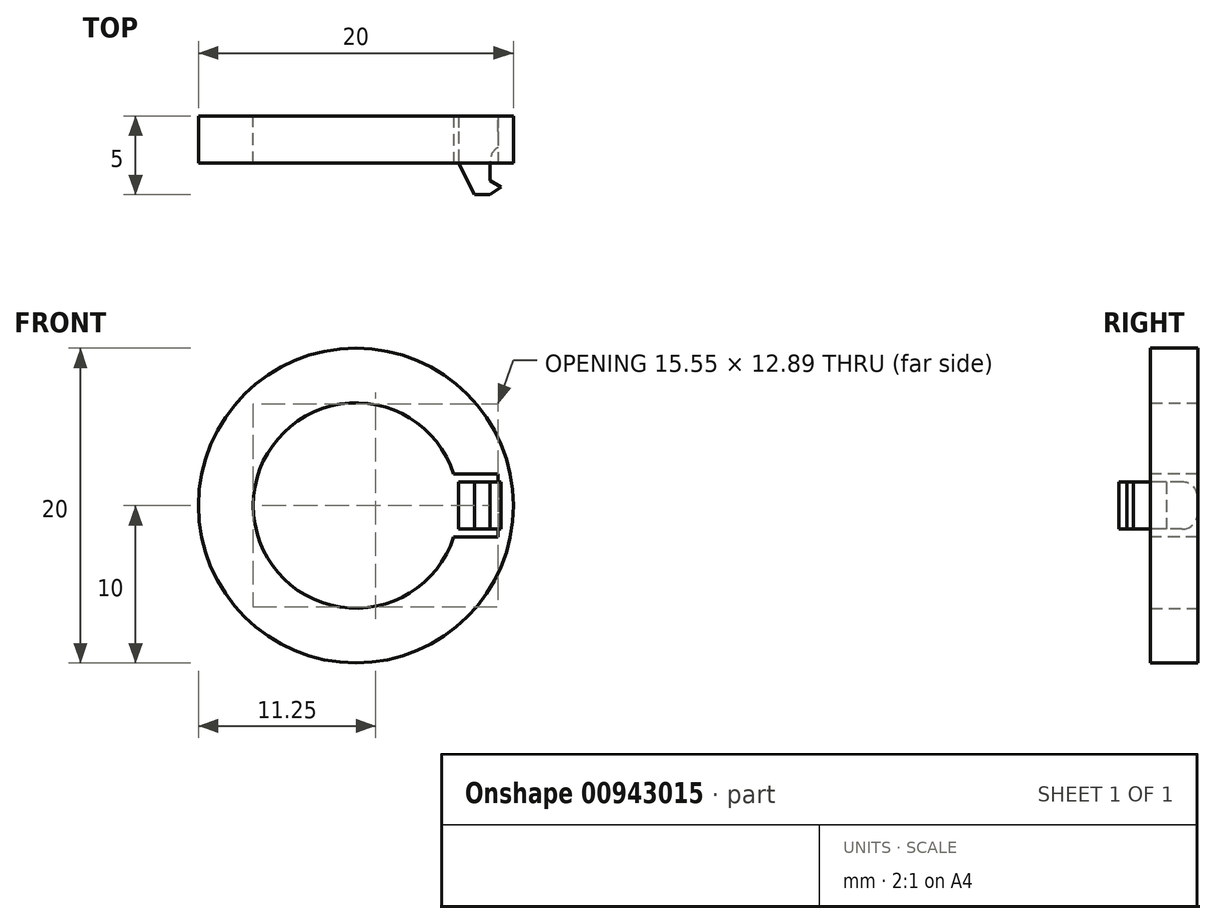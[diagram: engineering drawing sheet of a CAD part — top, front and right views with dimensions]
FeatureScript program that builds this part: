
annotation { "Feature Type Name" : "Feature", "Feature Type Description" : "" }
export const myFeature = defineFeature(function(context is Context, id is Id, definition is map)
    precondition{}
    {
        {
            var Q0;
            Q0=qCreatedBy(makeId("Front.planeOp"),FACE);
            var sketch = newSketch(context, id + "F0", { "sketchPlane" : qUnion([Q0])});
            skCircle(sketch, "E0", {"center": v(0, 0) * mm, "radius": 6.53 * mm});
            skCircle(sketch, "E1", {"center": v(0, 0) * mm, "radius": 10 * mm});
            skPoint(sketch, "E2", {"position": v(6.53, 0) * mm});
            skSolve(sketch);
        }
        {
            var Q0;
            Q0 = qSketchRegion(id + "F0", true);
            extrude(context, id + "F1", {"entities" : qUnion([Q0]), "depth" : 3 * mm, "offsetDistance" : 25 * mm});
        }
        {
            var Q0;
            Q0=qCreatedBy(makeId("Top.planeOp"),FACE);
            var sketch = newSketch(context, id + "F2", { "sketchPlane" : qUnion([Q0])});
            skLineSegment(sketch, "E3.bottom", {"start": v(6.53, -3) * mm, "end": v(8.53, -3) * mm});
            skLineSegment(sketch, "E3.top", {"start": v(7.53, -5) * mm, "end": v(8.53, -5) * mm});
            skLineSegment(sketch, "E3.left", {"start": v(6.53, -3) * mm, "end": v(7.53, -5) * mm});
            skLineSegment(sketch, "E3.right", {"start": v(8.53, -3) * mm, "end": v(8.53, -4.1) * mm});
            skLineSegment(sketch, "E4", {"start": v(8.53, -4.1) * mm, "end": v(9.23, -4.5) * mm});
            skLineSegment(sketch, "E5", {"start": v(9.23, -4.5) * mm, "end": v(8.53, -5) * mm});
            skLineSegment(sketch, "E6", {"start": v(0, 6.77) * mm, "end": v(0, -9.64) * mm, "construction": true});
            skSolve(sketch);
        }
        {
            var Q0;
            Q0=makeQuery(id+"F2.imprint","IMPRINT",FACE,{"disambiguationData":[TD([[makeQuery(id+"F2.imprint","IMPRINT",EDGE,{"derivedFrom":sQuery(id+"F2.wireOp",EDGE,"E3.bottom")}),-1.0]])]});
            extrude(context, id + "F3", {"entities" : qUnion([Q0]), "operationType" : NewBodyOperationType.ADD, "endBound" : BoundingType.SYMMETRIC, "depth" : 3 * mm, "offsetDistance" : 25 * mm});
        }
        {
            var Q0;
            Q0=makeQuery(id+"F1.opExtrude","CAP_FACE",FACE,{"disambiguationData":[OSD([sQuery(id+"F0.wireOp",EDGE,"E0"),sQuery(id+"F0.wireOp",EDGE,"E1")])],"isStart":false});
            var sketch = newSketch(context, id + "F4", { "sketchPlane" : qUnion([Q0])});
            skLineSegment(sketch, "E7", {"start": v(6.21, 2) * mm, "end": v(8.53, 2) * mm});
            skLineSegment(sketch, "E8", {"start": v(8.53, 2) * mm, "end": v(8.53, 1.5) * mm});
            skLineSegment(sketch, "E9.MirrorCS", {"start": v(6.21, -2) * mm, "end": v(8.53, -2) * mm});
            skLineSegment(sketch, "E10.MirrorCS", {"start": v(8.53, -2) * mm, "end": v(8.53, -1.5) * mm});
            skLineSegment(sketch, "E11", {"start": v(8.53, 2) * mm, "end": v(9.03, 2) * mm});
            skLineSegment(sketch, "E12", {"start": v(9.03, 2) * mm, "end": v(9.03, -2) * mm});
            skLineSegment(sketch, "E13", {"start": v(9.03, -2) * mm, "end": v(8.53, -2) * mm});
            skLineSegment(sketch, "E14", {"start": v(8.53, 1.5) * mm, "end": v(9.03, 1.5) * mm});
            skLineSegment(sketch, "E15", {"start": v(8.53, -1.5) * mm, "end": v(9.03, -1.5) * mm});
            skSolve(sketch);
        }
        {
            var Q0;
            {var subQ12=sQuery(id+"F4.wireOp",EDGE,"E7");Q0=makeQuery(id+"F4.imprint","IMPRINT",FACE,{"disambiguationData":[TD([[makeQuery(id+"F4.imprint","IMPRINT",EDGE,{"derivedFrom":subQ12}),-1.0]])]});}
            var Q1;
            {var subQ12=sQuery(id+"F4.wireOp",EDGE,"E9.MirrorCS");Q1=makeQuery(id+"F4.imprint","IMPRINT",FACE,{"disambiguationData":[TD([[makeQuery(id+"F4.imprint","IMPRINT",EDGE,{"derivedFrom":subQ12}),1.0]])]});}
            var Q2;
            Q2=makeQuery(id+"F4.imprint","IMPRINT",FACE,{"disambiguationData":[TD([[makeQuery(id+"F4.imprint","IMPRINT",EDGE,{"derivedFrom":sQuery(id+"F4.wireOp",EDGE,"E8")}),1.0]])]});
            var Q3;
            Q3=makeQuery(id+"F4.imprint","IMPRINT",FACE,{"disambiguationData":[TD([[makeQuery(id+"F4.imprint","IMPRINT",EDGE,{"derivedFrom":sQuery(id+"F4.wireOp",EDGE,"E10.MirrorCS")}),-1.0]])]});
            extrude(context, id + "F5", {"entities" : qUnion([Q0, Q1, Q2, Q3]), "operationType" : NewBodyOperationType.REMOVE, "oppositeDirection" : true, "depth" : 25 * mm, "offsetDistance" : 25 * mm});
        }
        {
            var Q0;
            {var subQ0=sQuery(id+"F4.wireOp",EDGE,"E14");Q0=makeQuery(id+"F4.imprint","IMPRINT",FACE,{"disambiguationData":[TD([[makeQuery(id+"F4.imprint","IMPRINT",EDGE,{"derivedFrom":subQ0}),-1.0]])]});}
            extrude(context, id + "F6", {"entities" : qUnion([Q0]), "operationType" : NewBodyOperationType.REMOVE, "oppositeDirection" : true, "depth" : 1 * mm, "offsetDistance" : 25 * mm});
        }
        {
            var Q0;
            {var subQ0=sQuery(id+"F0.wireOp",EDGE,"E0");var subQ2=sQuery(id+"F2.wireOp",EDGE,"E5");var subQ3=sQuery(id+"F2.wireOp",EDGE,"E4");var subQ4=sQuery(id+"F2.wireOp",EDGE,"E3.right");var subQ5=sQuery(id+"F2.wireOp",EDGE,"E3.left");var subQ6=sQuery(id+"F2.wireOp",EDGE,"E3.top");var subQ7=sQuery(id+"F2.wireOp",EDGE,"E3.bottom");var subQ8=sQuery(id+"F0.wireOp",EDGE,"E1");var subQ11=makeQuery(id+"F3.opExtrude","SWEPT_EDGE",EDGE,{"disambiguationData":[OSD([subQ7,subQ5])]});Q0=makeQuery(id+"F5.boolean.opBoolean","INTERSECT",EDGE,{"derivedFrom":[makeQuery(id+"F1.opExtrude","CAP_FACE",FACE,{"disambiguationData":[OSD([subQ0,subQ8])],"isStart":true}),makeQuery(id+"F5.opExtrude","SWEPT_FACE",FACE,{"disambiguationData":[OSD([subQ7,subQ5]),TDD([makeQuery(id+"F4.imprint","IMPRINT",EDGE,{"derivedFrom":makeQuery(id+"F3.boolean.opBoolean","SPLIT",EDGE,{"disambiguationData":[TD([makeQuery(id+"F3.opExtrude","CAP_FACE",FACE,{"disambiguationData":[OSD([subQ7,subQ6,subQ5,subQ4,subQ3,subQ2])],"isStart":true})])],"derivedFrom":subQ11})})])]}),makeQuery(id+"F5.opExtrude","SWEPT_FACE",FACE,{"disambiguationData":[OSD([subQ7,subQ5]),TDD([makeQuery(id+"F4.imprint","IMPRINT",EDGE,{"derivedFrom":makeQuery(id+"F3.boolean.opBoolean","SPLIT",EDGE,{"disambiguationData":[TD([makeQuery(id+"F3.opExtrude","CAP_FACE",FACE,{"disambiguationData":[OSD([subQ7,subQ6,subQ5,subQ4,subQ3,subQ2])],"isStart":false})])],"derivedFrom":subQ11})})])]})]});}
            fillet(context, id + "F7", {"entities" : qUnion([Q0]), "radius" : 1 * mm, "tangentPropagation" : true, "allowEdgeOverflow" : false});
        }
        {
            var Q0;
            Q0=makeQuery(id+"F6.boolean.opBoolean","COPY",EDGE,{"derivedFrom":makeQuery(id+"F6.opExtrude","CAP_EDGE",EDGE,{"disambiguationData":[OSD([sQuery(id+"F2.wireOp",EDGE,"E3.bottom"),sQuery(id+"F2.wireOp",EDGE,"E3.right")])],"isStart":false})});
            fillet(context, id + "F8", {"entities" : qUnion([Q0]), "radius" : 1 * mm, "tangentPropagation" : true, "allowEdgeOverflow" : false});
        }
        {
            var Q0;
            Q0=qCreatedBy(makeId("Front.planeOp"),FACE);
            cPlane(context, id + "F9", {"entities" : qUnion([Q0]), "cplaneType" : CPlaneType.OFFSET, "offset" : 25 * mm, "width" : 150 * mm, "height" : 150 * mm});
        }
        {
            var Q0;
            Q0=qCreatedBy(id+"F9.planeOp",FACE);
            var sketch = newSketch(context, id + "F10", { "sketchPlane" : qUnion([Q0])});
            skCircle(sketch, "E16", {"center": v(0, 0) * mm, "radius": 10 * mm});
            skCircle(sketch, "E17", {"center": v(0, 0) * mm, "radius": 6.55 * mm});
            skLineSegment(sketch, "E18", {"start": v(-1.75, 6.31) * mm, "end": v(-1.75, 8.61) * mm});
            skLineSegment(sketch, "E19", {"start": v(-1.75, 8.61) * mm, "end": v(1.75, 8.61) * mm});
            skLineSegment(sketch, "E20", {"start": v(1.75, 8.61) * mm, "end": v(1.75, 6.31) * mm});
            skLineSegment(sketch, "E21.1.0", {"start": v(-6.31, -1.75) * mm, "end": v(-8.61, -1.75) * mm});
            skLineSegment(sketch, "E21.1.1", {"start": v(-8.61, -1.75) * mm, "end": v(-8.61, 1.75) * mm});
            skLineSegment(sketch, "E21.1.2", {"start": v(-8.61, 1.75) * mm, "end": v(-6.31, 1.75) * mm});
            skLineSegment(sketch, "E21.2.0", {"start": v(1.75, -6.31) * mm, "end": v(1.75, -8.61) * mm});
            skLineSegment(sketch, "E21.2.1", {"start": v(1.75, -8.61) * mm, "end": v(-1.75, -8.61) * mm});
            skLineSegment(sketch, "E21.2.2", {"start": v(-1.75, -8.61) * mm, "end": v(-1.75, -6.31) * mm});
            skLineSegment(sketch, "E21.3.0", {"start": v(6.31, 1.75) * mm, "end": v(8.61, 1.75) * mm});
            skLineSegment(sketch, "E21.3.1", {"start": v(8.61, 1.75) * mm, "end": v(8.61, -1.75) * mm});
            skLineSegment(sketch, "E21.3.2", {"start": v(8.61, -1.75) * mm, "end": v(6.31, -1.75) * mm});
            skSolve(sketch);
        }
        {
            var Q0;
            Q0 = qSketchRegion(id + "F10", true);
            extrude(context, id + "F11", {"entities" : qUnion([Q0]), "depth" : 2 * mm, "offsetDistance" : 25 * mm});
        }
        {
            var Q0;
            Q0=makeQuery(id+"F11.opExtrude","CAP_FACE",FACE,{"disambiguationData":[OSD([sQuery(id+"F10.wireOp",EDGE,"E16"),sQuery(id+"F10.wireOp",EDGE,"E17"),sQuery(id+"F10.wireOp",EDGE,"E18"),sQuery(id+"F10.wireOp",EDGE,"E19"),sQuery(id+"F10.wireOp",EDGE,"E20"),sQuery(id+"F10.wireOp",EDGE,"E21.1.0"),sQuery(id+"F10.wireOp",EDGE,"E21.1.1"),sQuery(id+"F10.wireOp",EDGE,"E21.1.2"),sQuery(id+"F10.wireOp",EDGE,"E21.2.0"),sQuery(id+"F10.wireOp",EDGE,"E21.2.1"),sQuery(id+"F10.wireOp",EDGE,"E21.2.2"),sQuery(id+"F10.wireOp",EDGE,"E21.3.0"),sQuery(id+"F10.wireOp",EDGE,"E21.3.1"),sQuery(id+"F10.wireOp",EDGE,"E21.3.2")])],"isStart":false});
            var sketch = newSketch(context, id + "F12", { "sketchPlane" : qUnion([Q0])});
            skLineSegment(sketch, "E22", {"start": v(-1.75, 8.61) * mm, "end": v(-1.75, 9.61) * mm});
            skLineSegment(sketch, "E23", {"start": v(-1.75, 9.61) * mm, "end": v(1.75, 9.61) * mm});
            skLineSegment(sketch, "E24", {"start": v(1.75, 9.61) * mm, "end": v(1.75, 8.61) * mm});
            skLineSegment(sketch, "E25.1.0", {"start": v(-8.61, -1.75) * mm, "end": v(-9.61, -1.75) * mm});
            skLineSegment(sketch, "E25.1.1", {"start": v(-9.61, -1.75) * mm, "end": v(-9.61, 1.75) * mm});
            skLineSegment(sketch, "E25.1.2", {"start": v(-9.61, 1.75) * mm, "end": v(-8.61, 1.75) * mm});
            skLineSegment(sketch, "E25.2.0", {"start": v(1.75, -8.61) * mm, "end": v(1.75, -9.61) * mm});
            skLineSegment(sketch, "E25.2.1", {"start": v(1.75, -9.61) * mm, "end": v(-1.75, -9.61) * mm});
            skLineSegment(sketch, "E25.2.2", {"start": v(-1.75, -9.61) * mm, "end": v(-1.75, -8.61) * mm});
            skLineSegment(sketch, "E25.3.0", {"start": v(8.61, 1.75) * mm, "end": v(9.61, 1.75) * mm});
            skLineSegment(sketch, "E25.3.1", {"start": v(9.61, 1.75) * mm, "end": v(9.61, -1.75) * mm});
            skLineSegment(sketch, "E25.3.2", {"start": v(9.61, -1.75) * mm, "end": v(8.61, -1.75) * mm});
            skPoint(sketch, "E25.center", {"position": v(0, 0) * mm});
            skSolve(sketch);
        }
        {
            var Q0;
            Q0=makeQuery(id+"F12.imprint","IMPRINT",FACE,{"disambiguationData":[TD([[makeQuery(id+"F12.imprint","IMPRINT",EDGE,{"derivedFrom":sQuery(id+"F12.wireOp",EDGE,"E22")}),-1.0]])]});
            var Q1;
            Q1=makeQuery(id+"F12.imprint","IMPRINT",FACE,{"disambiguationData":[TD([[makeQuery(id+"F12.imprint","IMPRINT",EDGE,{"derivedFrom":sQuery(id+"F12.wireOp",EDGE,"E25.1.0")}),-1.0]])]});
            var Q2;
            Q2=makeQuery(id+"F12.imprint","IMPRINT",FACE,{"disambiguationData":[TD([[makeQuery(id+"F12.imprint","IMPRINT",EDGE,{"derivedFrom":sQuery(id+"F12.wireOp",EDGE,"E25.3.0")}),-1.0]])]});
            var Q3;
            Q3=makeQuery(id+"F12.imprint","IMPRINT",FACE,{"disambiguationData":[TD([[makeQuery(id+"F12.imprint","IMPRINT",EDGE,{"derivedFrom":sQuery(id+"F12.wireOp",EDGE,"E25.2.0")}),-1.0]])]});
            extrude(context, id + "F13", {"entities" : qUnion([Q0, Q1, Q2, Q3]), "operationType" : NewBodyOperationType.REMOVE, "oppositeDirection" : true, "depth" : 1 * mm, "offsetDistance" : 25 * mm});
        }
        {
            var Q0;
            Q0=qCreatedBy(id+"F9.planeOp",FACE);
            var sketch = newSketch(context, id + "F14", { "sketchPlane" : qUnion([Q0])});
            skCircle(sketch, "E26", {"center": v(0, 0) * mm, "radius": 10.98 * mm});
            skSolve(sketch);
        }
        {
            var Q0;
            Q0 = qSketchRegion(id + "F14", true);
            extrude(context, id + "F15", {"entities" : qUnion([Q0]), "depth" : 2 * mm, "offsetDistance" : 25 * mm});
        }
        {
            var Q0;
            Q0=makeQuery(id+"F11.opExtrude","SWEPT_BODY",BODY,{"disambiguationData":[OSD([sQuery(id+"F10.wireOp",EDGE,"E16"),sQuery(id+"F10.wireOp",EDGE,"E17"),sQuery(id+"F10.wireOp",EDGE,"E18"),sQuery(id+"F10.wireOp",EDGE,"E19"),sQuery(id+"F10.wireOp",EDGE,"E20"),sQuery(id+"F10.wireOp",EDGE,"E21.1.0"),sQuery(id+"F10.wireOp",EDGE,"E21.1.1"),sQuery(id+"F10.wireOp",EDGE,"E21.1.2"),sQuery(id+"F10.wireOp",EDGE,"E21.2.0"),sQuery(id+"F10.wireOp",EDGE,"E21.2.1"),sQuery(id+"F10.wireOp",EDGE,"E21.2.2"),sQuery(id+"F10.wireOp",EDGE,"E21.3.0"),sQuery(id+"F10.wireOp",EDGE,"E21.3.1"),sQuery(id+"F10.wireOp",EDGE,"E21.3.2")])]});
            var Q1;
            Q1=makeQuery(id+"F15.opExtrude","SWEPT_BODY",BODY,{"disambiguationData":[OSD([sQuery(id+"F14.wireOp",EDGE,"E26")])]});
            booleanBodies(context, id + "F16", {"operationType" : BooleanOperationType.SUBTRACTION, "tools" : qUnion([Q0]), "targets" : qUnion([Q1])});
        }
        {
            var Q0;
            Q0=makeQuery(id+"F16.opBoolean","SPLIT",BODY,{"disambiguationData":[OD(0.0)],"derivedFrom":makeQuery(id+"F15.opExtrude","SWEPT_BODY",BODY,{"disambiguationData":[OSD([sQuery(id+"F14.wireOp",EDGE,"E26")])]})});
            deleteBodies(context, id + "F17", {"entities" : qUnion([Q0])});
        }
    });
